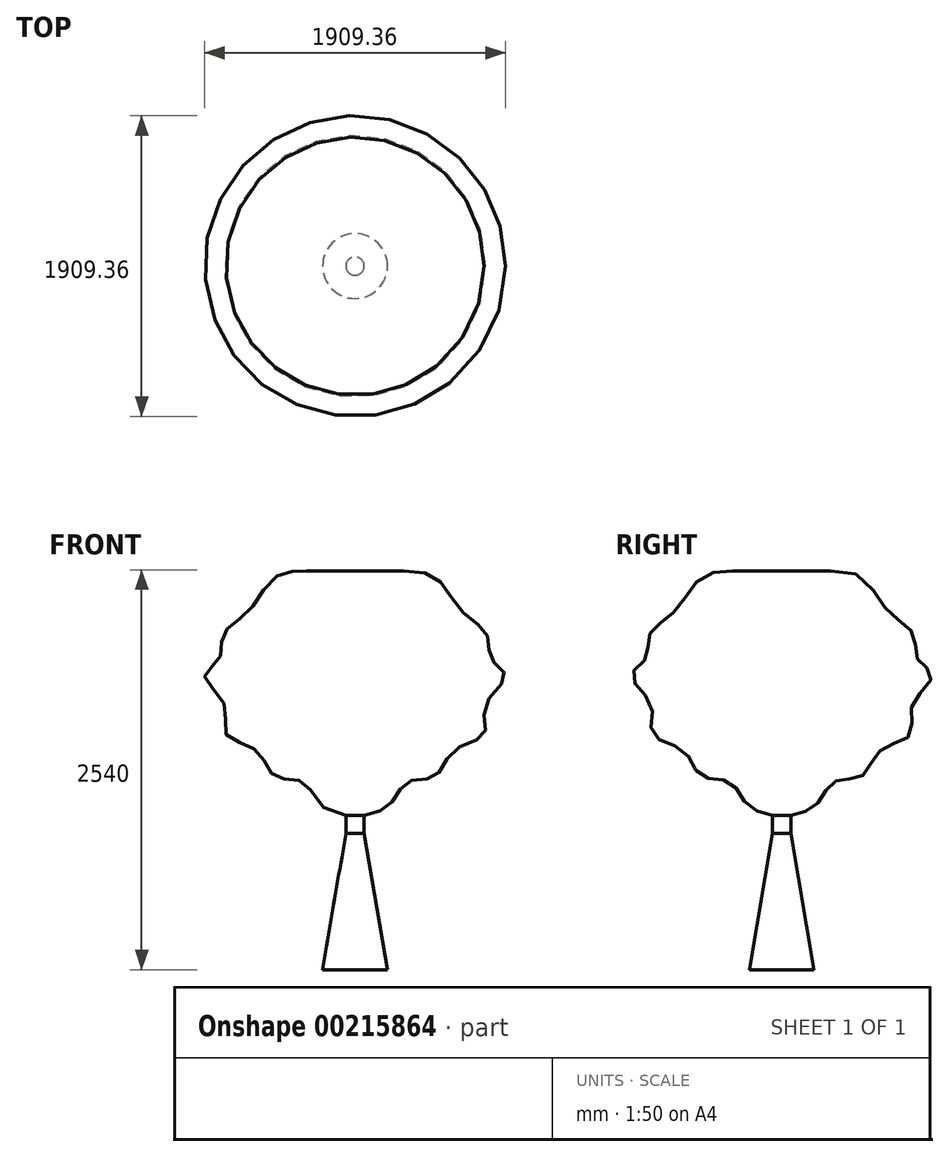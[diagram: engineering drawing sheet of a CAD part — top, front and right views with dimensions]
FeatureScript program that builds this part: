
annotation { "Feature Type Name" : "Feature", "Feature Type Description" : "" }
export const myFeature = defineFeature(function(context is Context, id is Id, definition is map)
    precondition{}
    {
        {
            var Q0;
            Q0=qCreatedBy(makeId("Front.planeOp"),FACE);
            var sketch = newSketch(context, id + "F0", { "sketchPlane" : qUnion([Q0])});
            skLineSegment(sketch, "E0", {"start": v(205.94, 0) * mm, "end": v(0, 0) * mm});
            skLineSegment(sketch, "E1", {"start": v(0, 0) * mm, "end": v(0, 2540) * mm});
            skLineSegment(sketch, "E2", {"start": v(58.41, 981.72) * mm, "end": v(58.41, 865.3) * mm});
            skLineSegment(sketch, "E3", {"start": v(58.41, 865.3) * mm, "end": v(205.94, 0) * mm});
            skFitSpline(sketch, "E4", {"points": [v(0, 2540) * mm, v(496.02, 2500.18) * mm, v(673.02, 2282.6) * mm, v(839.96, 2125.1) * mm, v(862.17, 1976.35) * mm, v(954.66, 1867.67) * mm, v(825.88, 1674.5) * mm, v(820.17, 1496.9) * mm, v(620.59, 1387.28) * mm, v(510.24, 1229.3) * mm, v(336.8, 1196.27) * mm, v(230.05, 1061.37) * mm, v(58.41, 981.72) * mm], "startDerivative": vector(5352.82, -583.73) * mm, "endDerivative": vector(-2661.22, -375.5) * mm});
            skSolve(sketch);
        }
        {
            var Q0;
            Q0 = qSketchRegion(id + "F0", true);
            var Q1;
            Q1=sQuery(id+"F0.wireOp",EDGE,"E1");
            revolve(context, id + "F1", {"entities" : qUnion([Q0]), "axis" : qUnion([Q1]), "revolveType" : RevolveType.FULL});
        }
    });
